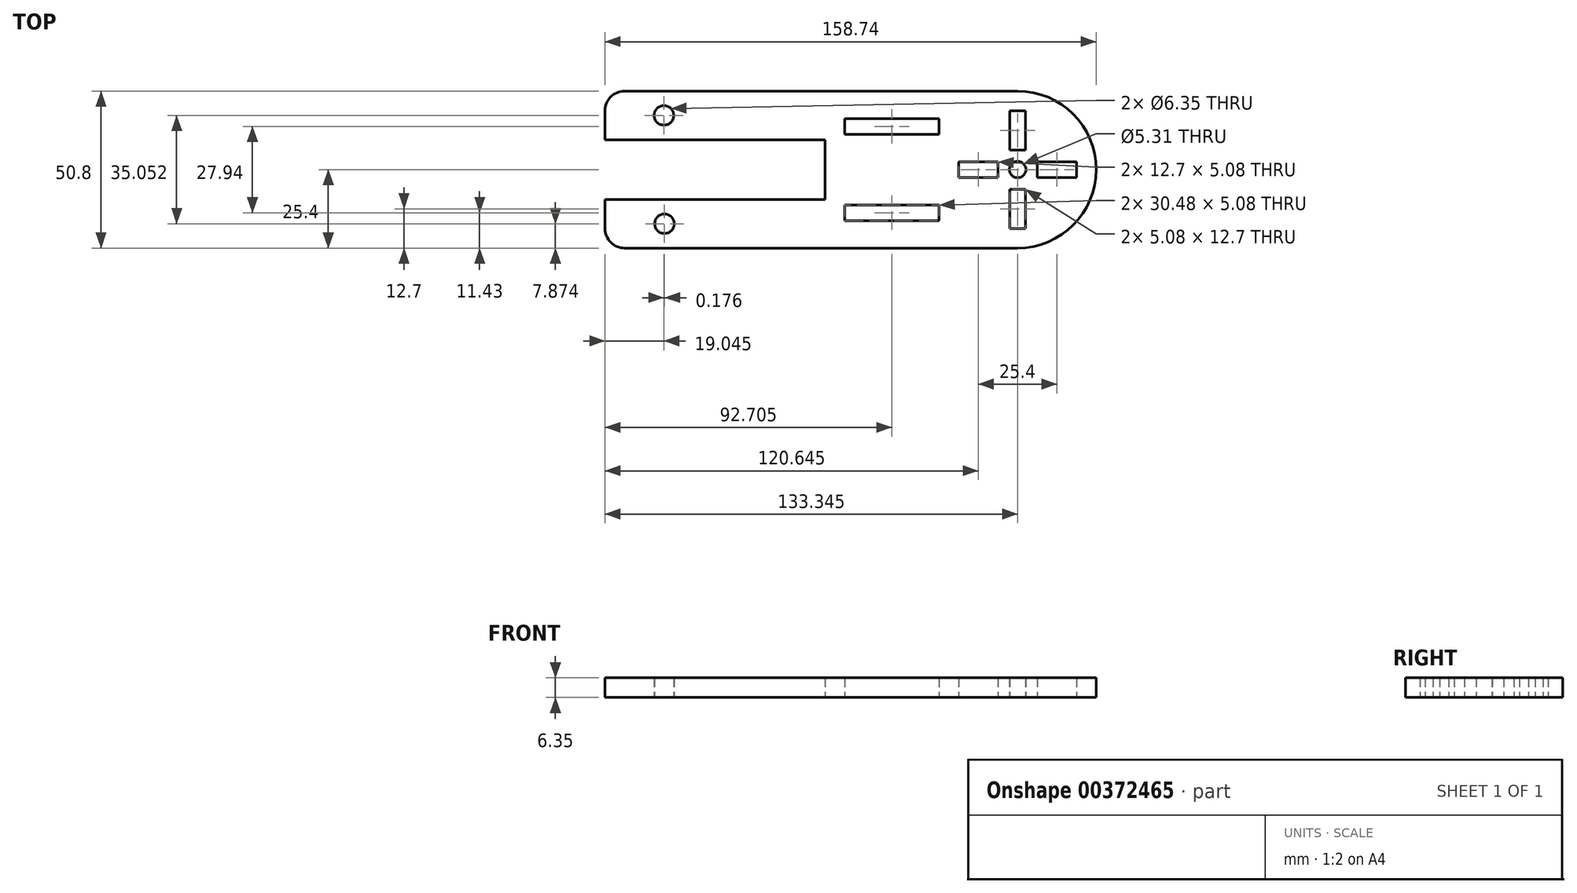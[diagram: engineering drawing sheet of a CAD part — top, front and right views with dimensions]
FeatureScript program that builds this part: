
annotation { "Feature Type Name" : "Feature", "Feature Type Description" : "" }
export const myFeature = defineFeature(function(context is Context, id is Id, definition is map)
    precondition{}
    {
        {
            var Q0;
            Q0=qCreatedBy(makeId("Top.planeOp"),FACE);
            var sketch = newSketch(context, id + "F0", { "sketchPlane" : qUnion([Q0])});
            skLineSegment(sketch, "E0.bottom", {"start": v(66.68, 25.4) * mm, "end": v(-60.33, 25.4) * mm});
            skLineSegment(sketch, "E0.top", {"start": v(66.68, -25.4) * mm, "end": v(-60.33, -25.4) * mm});
            skLineSegment(sketch, "E0.left", {"start": v(66.68, 25.4) * mm, "end": v(66.68, -25.4) * mm});
            skLineSegment(sketch, "E0.right", {"start": v(-66.68, 19.05) * mm, "end": v(-66.68, -19.05) * mm});
            skPoint(sketch, "E0.middle", {"position": v(0, 0) * mm});
            skArc(sketch, "E1", {"start": v(66.68, 25.4) * mm, "mid": v(92.08, 0) * mm, "end": v(66.68, -25.4) * mm});
            skCircle(sketch, "E2", {"center": v(66.68, 0) * mm, "radius": 2.65 * mm});
            skLineSegment(sketch, "E3.bottom", {"start": v(69.22, 19.05) * mm, "end": v(64.14, 19.05) * mm});
            skLineSegment(sketch, "E3.top", {"start": v(69.22, 6.35) * mm, "end": v(64.14, 6.35) * mm});
            skLineSegment(sketch, "E3.left", {"start": v(69.22, 19.05) * mm, "end": v(69.22, 6.35) * mm});
            skLineSegment(sketch, "E3.right", {"start": v(64.14, 19.05) * mm, "end": v(64.14, 6.35) * mm});
            skPoint(sketch, "E3.middle", {"position": v(66.68, 12.7) * mm});
            skLineSegment(sketch, "E4.bottom", {"start": v(69.22, -6.35) * mm, "end": v(64.14, -6.35) * mm});
            skLineSegment(sketch, "E4.top", {"start": v(69.22, -19.05) * mm, "end": v(64.14, -19.05) * mm});
            skLineSegment(sketch, "E4.left", {"start": v(69.22, -6.35) * mm, "end": v(69.22, -19.05) * mm});
            skLineSegment(sketch, "E4.right", {"start": v(64.14, -6.35) * mm, "end": v(64.14, -19.05) * mm});
            skPoint(sketch, "E4.middle", {"position": v(66.68, -12.7) * mm});
            skLineSegment(sketch, "E5.bottom", {"start": v(60.33, 2.54) * mm, "end": v(47.63, 2.54) * mm});
            skLineSegment(sketch, "E5.top", {"start": v(60.33, -2.54) * mm, "end": v(47.63, -2.54) * mm});
            skLineSegment(sketch, "E5.left", {"start": v(60.33, 2.54) * mm, "end": v(60.33, -2.54) * mm});
            skLineSegment(sketch, "E5.right", {"start": v(47.63, 2.54) * mm, "end": v(47.63, -2.54) * mm});
            skPoint(sketch, "E5.middle", {"position": v(53.98, 0) * mm});
            skLineSegment(sketch, "E6.bottom", {"start": v(85.73, 2.54) * mm, "end": v(73.03, 2.54) * mm});
            skLineSegment(sketch, "E6.top", {"start": v(85.73, -2.54) * mm, "end": v(73.03, -2.54) * mm});
            skLineSegment(sketch, "E6.left", {"start": v(85.73, 2.54) * mm, "end": v(85.73, -2.54) * mm});
            skLineSegment(sketch, "E6.right", {"start": v(73.03, 2.54) * mm, "end": v(73.03, -2.54) * mm});
            skPoint(sketch, "E6.middle", {"position": v(79.38, 0) * mm});
            skLineSegment(sketch, "E7.bottom", {"start": v(41.27, 11.43) * mm, "end": v(10.8, 11.43) * mm});
            skLineSegment(sketch, "E7.top", {"start": v(41.27, 16.51) * mm, "end": v(10.8, 16.51) * mm});
            skLineSegment(sketch, "E7.left", {"start": v(41.27, 11.43) * mm, "end": v(41.27, 16.51) * mm});
            skLineSegment(sketch, "E7.right", {"start": v(10.8, 11.43) * mm, "end": v(10.8, 16.51) * mm});
            skPoint(sketch, "E7.middle", {"position": v(26.03, 13.97) * mm});
            skLineSegment(sketch, "E8.bottom", {"start": v(41.27, -11.43) * mm, "end": v(10.8, -11.43) * mm});
            skLineSegment(sketch, "E8.top", {"start": v(41.27, -16.51) * mm, "end": v(10.8, -16.51) * mm});
            skLineSegment(sketch, "E8.left", {"start": v(41.27, -11.43) * mm, "end": v(41.27, -16.51) * mm});
            skLineSegment(sketch, "E8.right", {"start": v(10.8, -11.43) * mm, "end": v(10.8, -16.51) * mm});
            skPoint(sketch, "E8.middle", {"position": v(26.03, -13.97) * mm});
            skPoint(sketch, "E9", {"position": v(-66.68, 9.65) * mm});
            skPoint(sketch, "E10", {"position": v(-66.68, -9.65) * mm});
            skLineSegment(sketch, "E11.bottom", {"start": v(-66.68, 9.65) * mm, "end": v(4.44, 9.65) * mm});
            skLineSegment(sketch, "E11.top", {"start": v(-66.68, -9.65) * mm, "end": v(4.44, -9.65) * mm});
            skLineSegment(sketch, "E11.left", {"start": v(-66.68, 9.65) * mm, "end": v(-66.68, -9.65) * mm});
            skLineSegment(sketch, "E11.right", {"start": v(4.44, 9.65) * mm, "end": v(4.44, -9.65) * mm});
            skPoint(sketch, "E12.visualSharp", {"position": v(-66.67, 25.4) * mm});
            skArc(sketch, "E12.filletArc", {"start": v(-60.33, 25.4) * mm, "mid": v(-64.82, 23.54) * mm, "end": v(-66.68, 19.05) * mm});
            skPoint(sketch, "E13.visualSharp", {"position": v(-66.68, -25.4) * mm});
            skArc(sketch, "E13.filletArc", {"start": v(-66.68, -19.05) * mm, "mid": v(-64.82, -23.54) * mm, "end": v(-60.33, -25.4) * mm});
            skPoint(sketch, "E14", {"position": v(-47.63, 25.4) * mm});
            skCircle(sketch, "E15", {"center": v(-47.63, 17.53) * mm, "radius": 1.52 * mm});
            skPoint(sketch, "E16", {"position": v(-47.63, -25.4) * mm});
            skCircle(sketch, "E17", {"center": v(-47.45, -17.53) * mm, "radius": 3.18 * mm});
            skCircle(sketch, "E18", {"center": v(-47.63, 17.53) * mm, "radius": 3.18 * mm});
            skSolve(sketch);
        }
        {
            var Q0;
            Q0 = qSketchRegion(id + "F0", true);
            extrude(context, id + "F1", {"entities" : qUnion([Q0]), "depth" : 6.35 * mm});
        }
        {
            var Q0;
            Q0=makeQuery(id+"F1.opExtrude","CAP_FACE",FACE,{"disambiguationData":[OSD([sQuery(id+"F0.wireOp",EDGE,"E0.bottom"),sQuery(id+"F0.wireOp",EDGE,"E0.top"),sQuery(id+"F0.wireOp",EDGE,"E0.right"),sQuery(id+"F0.wireOp",EDGE,"E1"),sQuery(id+"F0.wireOp",EDGE,"E2"),sQuery(id+"F0.wireOp",EDGE,"E3.bottom"),sQuery(id+"F0.wireOp",EDGE,"E3.top"),sQuery(id+"F0.wireOp",EDGE,"E3.left"),sQuery(id+"F0.wireOp",EDGE,"E3.right"),sQuery(id+"F0.wireOp",EDGE,"E4.bottom"),sQuery(id+"F0.wireOp",EDGE,"E4.top"),sQuery(id+"F0.wireOp",EDGE,"E4.left"),sQuery(id+"F0.wireOp",EDGE,"E4.right"),sQuery(id+"F0.wireOp",EDGE,"E5.bottom"),sQuery(id+"F0.wireOp",EDGE,"E5.top"),sQuery(id+"F0.wireOp",EDGE,"E5.left"),sQuery(id+"F0.wireOp",EDGE,"E5.right"),sQuery(id+"F0.wireOp",EDGE,"E6.bottom"),sQuery(id+"F0.wireOp",EDGE,"E6.top"),sQuery(id+"F0.wireOp",EDGE,"E6.left"),sQuery(id+"F0.wireOp",EDGE,"E6.right"),sQuery(id+"F0.wireOp",EDGE,"E7.bottom"),sQuery(id+"F0.wireOp",EDGE,"E7.top"),sQuery(id+"F0.wireOp",EDGE,"E7.left"),sQuery(id+"F0.wireOp",EDGE,"E7.right"),sQuery(id+"F0.wireOp",EDGE,"E8.bottom"),sQuery(id+"F0.wireOp",EDGE,"E8.top"),sQuery(id+"F0.wireOp",EDGE,"E8.left"),sQuery(id+"F0.wireOp",EDGE,"E8.right")])],"isStart":false});
            extrude(context, id + "F2", {"entities" : qUnion([Q0]), "operationType" : NewBodyOperationType.ADD, "oppositeDirection" : true, "depth" : 6.35 * mm});
        }
        {
            var Q0;
            Q0=makeQuery(id+"F0.imprint","IMPRINT",FACE,{"disambiguationData":[TD([[makeQuery(id+"F0.imprint","IMPRINT",EDGE,{"derivedFrom":sQuery(id+"F0.wireOp",EDGE,"E11.bottom")}),-1.0]])]});
            extrude(context, id + "F3", {"entities" : qUnion([Q0]), "operationType" : NewBodyOperationType.REMOVE, "depth" : 93.98 * mm});
        }
    });
